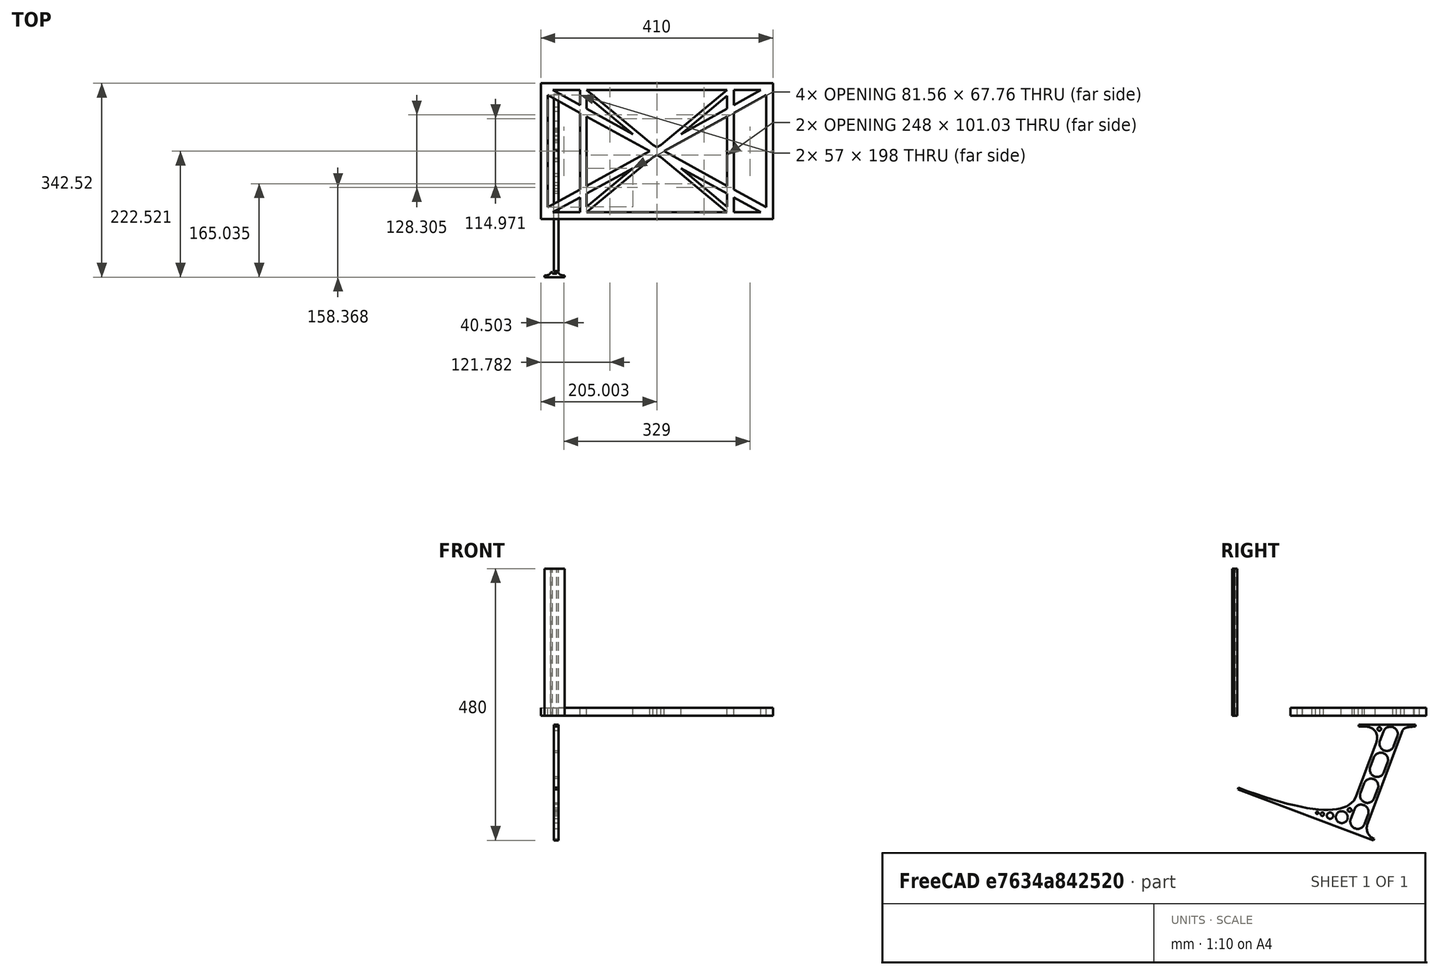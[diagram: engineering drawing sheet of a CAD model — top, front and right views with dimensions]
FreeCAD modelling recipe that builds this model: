
FCSTD DOCUMENT  (FreeCAD 0.19R0.19.2)
Label: laptopStand049
License: All rights reserved
LicenseURL: http://en.wikipedia.org/wiki/All_rights_reserved
objects: Sketcher::SketchObject×3, Part::Extrusion×3
note: 6 computed .brp shape members not serialized (recipe doc carries the construction recipe); baked Part::Feature solids carry a one-line shape summary decoded from their .brp

FEATURE [Sketcher::SketchObject] Sketch
  FullyConstrained = false
  sketch-geometry (73):
    g0: LineSegment StartX=-22.9272 StartY=136.221 StartZ=0 EndX=387.073 EndY=136.221 EndZ=0
    g1: LineSegment StartX=-22.9272 StartY=-103.779 StartZ=0 EndX=387.073 EndY=-103.779 EndZ=0
    g2: LineSegment StartX=375.073 StartY=115.221 StartZ=0 EndX=318.073 EndY=83.9235 EndZ=0
    g3: LineSegment StartX=-10.9272 StartY=-82.7794 StartZ=0 EndX=46.0728 EndY=-51.4823 EndZ=0
    g4: LineSegment StartX=-1.92719 StartY=124.221 StartZ=0 EndX=46.0728 EndY=97.8651 EndZ=0
    g5: LineSegment StartX=366.073 StartY=-91.7794 StartZ=0 EndX=318.073 EndY=-65.424 EndZ=0
    g6: LineSegment StartX=-10.9272 StartY=115.221 StartZ=0 EndX=-10.9272 EndY=-82.7794 EndZ=0
    g7: LineSegment StartX=375.073 StartY=-82.7794 StartZ=0 EndX=375.073 EndY=115.221 EndZ=0
    g8: LineSegment StartX=-1.92719 StartY=-91.7794 StartZ=0 EndX=46.0728 EndY=-91.7794 EndZ=0
    g9: LineSegment StartX=318.073 StartY=124.221 StartZ=0 EndX=366.073 EndY=124.221 EndZ=0
    g10: LineSegment StartX=306.073 StartY=-81.8102 StartZ=0 EndX=224.513 EndY=-14.0532 EndZ=0
    g11: LineSegment StartX=58.0728 StartY=114.251 StartZ=0 EndX=139.632 EndY=46.4944 EndZ=0
    g12: LineSegment StartX=306.073 StartY=124.221 StartZ=0 EndX=189.124 EndY=27.0628 EndZ=0
    g13: LineSegment StartX=58.0728 StartY=-91.7794 StartZ=0 EndX=175.022 EndY=5.37834 EndZ=0
    g14: LineSegment StartX=46.0728 StartY=124.221 StartZ=0 EndX=46.0728 EndY=97.8651 EndZ=0
    g15: LineSegment StartX=58.0728 StartY=-81.8102 StartZ=0 EndX=58.0728 EndY=-58.8351 EndZ=0
    g16: LineSegment StartX=318.073 StartY=124.221 StartZ=0 EndX=318.073 EndY=97.8651 EndZ=0
    g17: LineSegment StartX=306.073 StartY=114.251 StartZ=0 EndX=306.073 EndY=91.2763 EndZ=0
    g18: LineSegment StartX=224.513 StartY=46.4944 StartZ=0 EndX=306.073 EndY=114.251 EndZ=0
    g19: LineSegment StartX=175.022 StartY=27.0628 StartZ=0 EndX=58.0728 EndY=124.221 EndZ=0
    g20: LineSegment StartX=169.377 StartY=16.2206 StartZ=0 EndX=58.0728 EndY=77.3346 EndZ=0
    g21: LineSegment StartX=139.632 StartY=-14.0532 StartZ=0 EndX=58.0728 EndY=-81.8102 EndZ=0
    g22: LineSegment StartX=194.768 StartY=16.2206 StartZ=0 EndX=306.073 EndY=-44.8935 EndZ=0
    g23: LineSegment StartX=224.513 StartY=46.4944 StartZ=0 EndX=306.073 EndY=91.2763 EndZ=0
    g24: LineSegment StartX=175.022 StartY=27.0628 StartZ=0 EndX=179.022 EndY=24.8665 EndZ=0
    g25: LineSegment StartX=139.632 StartY=-14.0532 StartZ=0 EndX=58.0728 EndY=-58.8351 EndZ=0
    g26: LineSegment StartX=189.124 StartY=5.37834 StartZ=0 EndX=185.124 EndY=7.57463 EndZ=0
    g27: LineSegment StartX=189.124 StartY=5.37834 StartZ=0 EndX=306.073 EndY=-91.7794 EndZ=0
    g28: LineSegment StartX=306.073 StartY=77.3346 StartZ=0 EndX=306.073 EndY=-44.8935 EndZ=0
    g29: LineSegment StartX=318.073 StartY=83.9235 StartZ=0 EndX=318.073 EndY=-51.4823 EndZ=0
    g30: LineSegment StartX=318.073 StartY=97.8651 StartZ=0 EndX=366.073 EndY=124.221 EndZ=0
    g31: LineSegment StartX=306.073 StartY=77.3346 StartZ=0 EndX=194.768 EndY=16.2206 EndZ=0
    g32: LineSegment StartX=306.073 StartY=-58.8351 StartZ=0 EndX=224.513 EndY=-14.0532 EndZ=0
    g33: LineSegment StartX=306.073 StartY=-58.8351 StartZ=0 EndX=306.073 EndY=-81.8102 EndZ=0
    g34: LineSegment StartX=318.073 StartY=-51.4823 StartZ=0 EndX=375.073 EndY=-82.7794 EndZ=0
    g35: LineSegment StartX=318.073 StartY=-65.424 StartZ=0 EndX=318.073 EndY=-91.7794 EndZ=0
    g36: LineSegment StartX=318.073 StartY=-91.7794 StartZ=0 EndX=366.073 EndY=-91.7794 EndZ=0
    g37: LineSegment StartX=58.0728 StartY=-44.8935 StartZ=0 EndX=58.0728 EndY=77.3346 EndZ=0
    g38: LineSegment StartX=46.0728 StartY=-65.424 StartZ=0 EndX=-1.92719 EndY=-91.7794 EndZ=0
    g39: LineSegment StartX=46.0728 StartY=-65.424 StartZ=0 EndX=46.0728 EndY=-91.7794 EndZ=0
    g40: LineSegment StartX=58.0728 StartY=-44.8935 StartZ=0 EndX=169.377 EndY=16.2206 EndZ=0
    g41: LineSegment StartX=58.0728 StartY=91.2763 StartZ=0 EndX=58.0728 EndY=114.251 EndZ=0
    g42: LineSegment StartX=46.0728 StartY=83.9235 StartZ=0 EndX=46.0728 EndY=-51.4823 EndZ=0
    g43: LineSegment StartX=46.0728 StartY=124.221 StartZ=0 EndX=-1.92719 EndY=124.221 EndZ=0
    g44: LineSegment StartX=58.0728 StartY=91.2763 StartZ=0 EndX=139.632 EndY=46.4944 EndZ=0
    g45: LineSegment StartX=46.0728 StartY=83.9235 StartZ=0 EndX=-10.9272 EndY=115.221 EndZ=0
    g46: LineSegment StartX=-22.9272 StartY=136.221 StartZ=0 EndX=-42.9272 EndY=136.221 EndZ=0
    g47: LineSegment StartX=387.073 StartY=136.221 StartZ=0 EndX=407.073 EndY=136.221 EndZ=0
    g48: LineSegment StartX=-42.9272 StartY=136.221 StartZ=0 EndX=-42.9272 EndY=-103.779 EndZ=0
    g49: LineSegment StartX=-22.9272 StartY=-103.779 StartZ=0 EndX=-42.9272 EndY=-103.779 EndZ=0
    g50: LineSegment StartX=407.073 StartY=136.221 StartZ=0 EndX=407.073 EndY=-103.779 EndZ=0
    g51: LineSegment StartX=387.073 StartY=-103.779 StartZ=0 EndX=407.073 EndY=-103.779 EndZ=0
    g52: LineSegment StartX=179.022 StartY=27.0628 StartZ=0 EndX=179.022 EndY=124.221 EndZ=0
    g53: LineSegment StartX=185.124 StartY=27.0628 StartZ=0 EndX=185.124 EndY=124.221 EndZ=0
    g54: LineSegment StartX=179.022 StartY=27.0628 StartZ=0 EndX=179.022 EndY=24.8665 EndZ=0
    g55: LineSegment StartX=185.124 StartY=27.0628 StartZ=0 EndX=185.124 EndY=24.8665 EndZ=0
    g56: LineSegment StartX=185.124 StartY=7.57463 StartZ=0 EndX=185.124 EndY=-91.7794 EndZ=0
    g57: LineSegment StartX=179.022 StartY=7.57463 StartZ=0 EndX=179.022 EndY=-91.7794 EndZ=0
    g58: LineSegment StartX=189.124 StartY=27.0628 StartZ=0 EndX=185.124 EndY=24.8665 EndZ=0
    g59: LineSegment StartX=175.022 StartY=5.37834 StartZ=0 EndX=179.022 EndY=7.57463 EndZ=0
    g60: ArcOfCircle CenterX=-26.9272 CenterY=22.1087 CenterZ=0 NormalX=0 NormalY=0 NormalZ=1 AngleXU=0 Radius=8 StartAngle=1e-16 EndAngle=3.14159
    g61: ArcOfCircle CenterX=-26.9272 CenterY=-83.7794 CenterZ=0 NormalX=0 NormalY=0 NormalZ=1 AngleXU=0 Radius=8 StartAngle=3.14159 EndAngle=6.28319
    g62: LineSegment StartX=-34.9272 StartY=22.1087 StartZ=0 EndX=-34.9272 EndY=-83.7794 EndZ=0
    g63: LineSegment StartX=-18.9272 StartY=22.1087 StartZ=0 EndX=-18.9272 EndY=-83.7794 EndZ=0
    g64: LineSegment StartX=391.073 StartY=-91.7794 StartZ=0 EndX=391.073 EndY=-83.7794 EndZ=0
    g65: LineSegment StartX=185.124 StartY=-91.7794 StartZ=0 EndX=306.073 EndY=-91.7794 EndZ=0
    g66: LineSegment StartX=179.022 StartY=-91.7794 StartZ=0 EndX=58.0728 EndY=-91.7794 EndZ=0
    g67: LineSegment StartX=306.073 StartY=124.221 StartZ=0 EndX=185.124 EndY=124.221 EndZ=0
    g68: LineSegment StartX=179.022 StartY=124.221 StartZ=0 EndX=58.0728 EndY=124.221 EndZ=0
    g69: ArcOfCircle CenterX=451.856 CenterY=33.5494 CenterZ=0 NormalX=0 NormalY=0 NormalZ=1 AngleXU=0 Radius=8 StartAngle=-1.8e-15 EndAngle=3.14159
    g70: ArcOfCircle CenterX=451.856 CenterY=-72.3387 CenterZ=0 NormalX=0 NormalY=0 NormalZ=1 AngleXU=0 Radius=8 StartAngle=3.14159 EndAngle=6.28319
    g71: LineSegment StartX=459.856 StartY=33.5494 StartZ=0 EndX=459.856 EndY=-72.3387 EndZ=0
    g72: LineSegment StartX=443.856 StartY=33.5494 StartZ=0 EndX=443.856 EndY=-72.3387 EndZ=0
  constraints (147):
    c: Horizontal(g0)
    c: Distance(g0) = 410
    c: Horizontal(g1)
    c: Block(g0)
    c: Horizontal(g8)
    c: Horizontal(g9)
    c: Tangent(g5,g20)
    c: PointOnObject(g20,g3)
    c: PointOnObject(g22,g2)
    c: Coincident(g44,g11)
    c: Coincident(g24,g19)
    c: Coincident(g18,g23)
    c: Coincident(g25,g21)
    c: Coincident(g32,g10)
    c: Coincident(g27,g26)
    c: Coincident(g18,g17)
    c: Tangent(g17,g28)
    c: Tangent(g16,g29)
    c: Coincident(g23,g17)
    c: Tangent(g23,g30)
    c: Coincident(g2,g29)
    c: Coincident(g31,g28)
    c: Tangent(g2,g31)
    c: Coincident(g33,g10)
    c: Tangent(g5,g32)
    c: Tangent(g28,g33)
    c: Coincident(g22,g28)
    c: Tangent(g22,g34)
    c: Coincident(g29,g34)
    c: Coincident(g35,g5)
    c: Tangent(g29,g35)
    c: Coincident(g21,g15)
    c: Tangent(g15,g37)
    c: Coincident(g25,g15)
    c: Tangent(g25,g38)
    c: Coincident(g39,g38)
    c: Tangent(g14,g39)
    c: Coincident(g3,g42)
    c: Coincident(g40,g37)
    c: Tangent(g3,g40)
    c: Tangent(g37,g41)
    c: Tangent(g14,g42)
    c: Coincident(g11,g41)
    c: Coincident(g4,g14)
    c: Coincident(g44,g41)
    c: Tangent(g4,g44)
    c: Coincident(g20,g37)
    c: Coincident(g45,g42)
    c: Tangent(g20,g45)
    c: Block(g19)
    c: Block(g12)
    c: Block(g16)
    c: Block(g30)
    c: Block(g2)
    c: Block(g34)
    c: Block(g7)
    c: Block(g32)
    c: Block(g33)
    c: Block(g5)
    c: Block(g35)
    c: Block(g18)
    c: Block(g27)
    c: Block(g13)
    c: Block(g25)
    c: Block(g21)
    c: Block(g39)
    c: Block(g38)
    c: Block(g3)
    c: Block(g6)
    c: Block(g45)
    c: Block(g4)
    c: Block(g14)
    c: Block(g11)
    c: Block(g41)
    c: Block(g31)
    c: Block(g28)
    c: Block(g20)
    c: Block(g40)
    c: Block(g43)
    c: Block(g9)
    c: Block(g36)
    c: Block(g8)
    c: Horizontal(g46)
    c: Distance(g46) = 20
    c: Coincident(g47,g0)
    c: Horizontal(g47)
    c: Distance(g47) = 20
    c: Coincident(g48,g46)
    c: Vertical(g48)
    c: Horizontal(g49)
    c: Coincident(g49,g48)
    c: Coincident(g50,g47)
    c: Vertical(g50)
    c: Coincident(g51,g1)
    c: Horizontal(g51)
    c: Coincident(g51,g50)
    c: Block(g50)
    c: Block(g49)
    c: Block(g48)
    c: Block(g1)
    c: Vertical(g52)
    c: Vertical(g53)
    c: Vertical(g54)
    c: Vertical(g55)
    c: Tangent(g55,g56)
    c: Tangent(g54,g57)
    c: Coincident(g24,g54)
    c: Coincident(g26,g56)
    c: Block(g52)
    c: Block(g53)
    c: Block(g57)
    c: Block(g56)
    c: Coincident(g58,g12)
    c: Coincident(g58,g55)
    c: Coincident(g59,g13)
    c: Coincident(g59,g57)
    c: Tangent(g60,g63) = 1.5708
    c: Tangent(g60,g62) = -1.5708
    c: Tangent(g62,g61) = -1.5708
    c: Tangent(g63,g61) = 1.5708
    c: Vertical(g62)
    c: Equal(g60,g61)
    c: Block(g63)
    c: Block(g62)
    c: Vertical(g64)
    c: Distance(g64) = 8
    c: Coincident(g65,g56)
    c: Coincident(g65,g27)
    c: Horizontal(g65)
    c: Coincident(g66,g57)
    c: Coincident(g66,g13)
    c: Horizontal(g66)
    c: Coincident(g67,g12)
    c: Coincident(g67,g53)
    c: Horizontal(g67)
    c: Coincident(g68,g52)
    c: Coincident(g68,g19)
    c: Horizontal(g68)
    c: Tangent(g69,g71) = 1.5708
    c: Tangent(g71,g70) = 1.5708
    c: Equal(g69,g70)
    c: Distance(g51) = 20
    c: Distance(g1) = 410
    c: Coincident(g72,g69)
    c: Coincident(g72,g70)
    c: Vertical(g72)
    c: Block(g64)
FEATURE [Sketcher::SketchObject] Sketch001
  FullyConstrained = true
  MapMode = 4
  Placement = pos=(0,0,0) rot=(0.57735,0.57735,0.57735;2.0944rad)
  Support = -> [Sketch]
  sketch-geometry (46):
    g0: BSplineCurve PolesCount=3 KnotsCount=2 Degree=2 IsPeriodic=0
    g1: ArcOfCircle CenterX=73.122 CenterY=-32.2909 CenterZ=0 NormalX=0 NormalY=0 NormalZ=1 AngleXU=0 Radius=13 StartAngle=5.92268 EndAngle=9.06428
    g2: ArcOfCircle CenterX=66.7816 CenterY=-49.1439 CenterZ=0 NormalX=0 NormalY=0 NormalZ=1 AngleXU=0 Radius=13 StartAngle=2.78068 EndAngle=5.92131
    g3: ArcOfCircle CenterX=55.9263 CenterY=-78.1807 CenterZ=0 NormalX=0 NormalY=0 NormalZ=1 AngleXU=0 Radius=13 StartAngle=5.92268 EndAngle=9.06428
    g4: ArcOfCircle CenterX=49.5884 CenterY=-95.0342 CenterZ=0 NormalX=0 NormalY=0 NormalZ=1 AngleXU=0 Radius=13 StartAngle=2.78068 EndAngle=5.92131
    g5: ArcOfCircle CenterX=38.7206 CenterY=-124.067 CenterZ=0 NormalX=0 NormalY=0 NormalZ=1 AngleXU=0 Radius=13 StartAngle=5.92268 EndAngle=9.06428
    g6: ArcOfCircle CenterX=32.3875 CenterY=-140.92 CenterZ=0 NormalX=0 NormalY=0 NormalZ=1 AngleXU=0 Radius=13 StartAngle=2.78068 EndAngle=5.92131
    g7: ArcOfCircle CenterX=21.4715 CenterY=-169.934 CenterZ=0 NormalX=0 NormalY=0 NormalZ=1 AngleXU=0 Radius=13 StartAngle=5.92268 EndAngle=9.06428
    g8: ArcOfCircle CenterX=15.1336 CenterY=-186.787 CenterZ=0 NormalX=0 NormalY=0 NormalZ=1 AngleXU=0 Radius=13 StartAngle=2.78068 EndAngle=5.92131
    g9-g12: Circle x4 (B-spline internal-alignment scaffolding for g13; pole/knot coordinates omitted)
    g13: BSplineCurve PolesCount=4 KnotsCount=2 Degree=3 IsPeriodic=0
    g14: GeomPoint X=28.8094 Y=-19.0875 Z=0
    g15: GeomPoint X=47.0443 Y=-50.4712 Z=0
    g16: Circle CenterX=53.5586 CenterY=-23.2695 CenterZ=0 NormalX=0 NormalY=0 NormalZ=1 AngleXU=0 Radius=3.24518
    g17: Circle CenterX=-195.441 CenterY=-127.082 CenterZ=0 NormalX=0 NormalY=0 NormalZ=1 AngleXU=0 Radius=1
    g18: Circle CenterX=-8.24091 CenterY=-197.481 CenterZ=0 NormalX=0 NormalY=0 NormalZ=1 AngleXU=0 Radius=1
    g19: Circle CenterX=12.8789 CenterY=-141.321 CenterZ=0 NormalX=0 NormalY=0 NormalZ=1 AngleXU=0 Radius=1
    g20: BSplineCurve PolesCount=3 KnotsCount=2 Degree=2 IsPeriodic=0
    g21: GeomPoint X=-195.441 Y=-127.082 Z=0
    g22: GeomPoint X=12.8789 Y=-141.321 Z=0
    g23: Circle CenterX=-12.8016 CenterY=-179.036 CenterZ=0 NormalX=0 NormalY=0 NormalZ=1 AngleXU=0 Radius=10.5072
    g24: Circle CenterX=0.933922 CenterY=-166.43 CenterZ=0 NormalX=0 NormalY=0 NormalZ=1 AngleXU=0 Radius=3.26661
    g25: Circle CenterX=-33.5518 CenterY=-176.44 CenterZ=0 NormalX=0 NormalY=0 NormalZ=1 AngleXU=0 Radius=5.64388
    g26: Circle CenterX=-47.2366 CenterY=-173.859 CenterZ=0 NormalX=0 NormalY=0 NormalZ=1 AngleXU=0 Radius=3.01653
    g27: Circle CenterX=-56.2595 CenterY=-171.456 CenterZ=0 NormalX=0 NormalY=0 NormalZ=1 AngleXU=0 Radius=2.12826
    g28: ArcOfCircle CenterX=51.2151 CenterY=-198.473 CenterZ=0 NormalX=0 NormalY=0 NormalZ=1 AngleXU=0 Radius=20 StartAngle=2.78189 EndAngle=4.35269
    g29: LineSegment StartX=32.4951 StartY=-191.433 StartZ=0 EndX=94.6577 EndY=-26.1351 EndZ=0
    g30: LineSegment StartX=43.1192 StartY=-220.001 StartZ=0 EndX=-196.497 EndY=-129.89 EndZ=0
    g31: LineSegment StartX=43.1192 StartY=-220.001 StartZ=0 EndX=44.1752 EndY=-217.193 EndZ=0
    g32: LineSegment StartX=117.223 StartY=-19.0875 StartZ=0 EndX=117.223 EndY=-16.0875 EndZ=0
    g33: LineSegment StartX=117.223 StartY=-16.0875 StartZ=0 EndX=17.2232 EndY=-16.0875 EndZ=0
    g34: LineSegment StartX=17.2232 StartY=-16.0875 StartZ=0 EndX=17.2232 EndY=-19.0875 EndZ=0
    g35: LineSegment StartX=28.8094 StartY=-19.0875 StartZ=0 EndX=17.2232 EndY=-19.0875 EndZ=0
    g36: LineSegment StartX=47.0443 StartY=-50.4712 StartZ=0 EndX=12.8789 EndY=-141.321 EndZ=0
    g37: LineSegment StartX=-195.441 StartY=-127.082 StartZ=0 EndX=-196.497 EndY=-129.89 EndZ=0
    g38: LineSegment StartX=85.2864 StartY=-36.8765 StartZ=0 EndX=78.9396 EndY=-53.7463 EndZ=0
    g39: LineSegment StartX=60.9577 StartY=-27.7052 StartZ=0 EndX=54.6191 EndY=-44.5532 EndZ=0
    g40: LineSegment StartX=68.0907 StartY=-82.7664 StartZ=0 EndX=61.7465 EndY=-99.6365 EndZ=0
    g41: LineSegment StartX=43.7619 StartY=-73.595 StartZ=0 EndX=37.426 EndY=-90.4435 EndZ=0
    g42: LineSegment StartX=50.885 StartY=-128.652 StartZ=0 EndX=44.5456 EndY=-145.522 EndZ=0
    g43: LineSegment StartX=26.5562 StartY=-119.481 StartZ=0 EndX=20.2251 EndY=-136.329 EndZ=0
    g44: LineSegment StartX=9.3071 StartY=-165.349 StartZ=0 EndX=2.97115 EndY=-182.197 EndZ=0
    g45: LineSegment StartX=33.6358 StartY=-174.52 StartZ=0 EndX=27.2917 EndY=-191.39 EndZ=0
  constraints (70):
    c: Block(g0)
    c: Block(g1)
    c: Block(g2)
    c: Block(g4)
    c: Block(g3)
    c: Block(g6)
    c: Block(g5)
    c: Block(g8)
    c: Block(g7)
    c: Weight(g9) = 1
    c: Equal(g9,g10)
    c: Equal(g9,g11)
    c: Equal(g9,g12)
    c: InternalAlignment(g9-g12 -> g13) x4
    c: InternalAlignment(g14,g13)
    c: InternalAlignment(g15,g13)
    c: Block(g16)
    c: Weight(g17) = 1
    c: Equal(g17,g18)
    c: Equal(g17,g19)
    c: InternalAlignment(g17,g20)
    c: InternalAlignment(g18,g20)
    c: InternalAlignment(g19,g20)
    c: InternalAlignment(g21,g20)
    c: InternalAlignment(g22,g20)
    c: Block(g20)
    c: Block(g23)
    c: Block(g24)
    c: Block(g25)
    c: Block(g26)
    c: Block(g27)
    c: Block(g28)
    c: Coincident(g29,g28)
    c: Coincident(g29,g0)
    c: Block(g13)
    c: Coincident(g31,g30)
    c: Coincident(g31,g28)
    c: Block(g31)
    c: Coincident(g32,g0)
    c: Vertical(g32)
    c: Coincident(g33,g32)
    c: Horizontal(g33)
    c: Coincident(g34,g33)
    c: Vertical(g34)
    c: Block(g33)
    c: Coincident(g35,g13)
    c: Coincident(g35,g34)
    c: Horizontal(g35)
    c: Coincident(g36,g13)
    c: Coincident(g36,g20)
    c: Coincident(g37,g20)
    c: Coincident(g37,g30)
    c: Block(g30)
    c: Coincident(g38,g1)
    c: Coincident(g38,g2)
    c: Coincident(g39,g1)
    c: Coincident(g39,g2)
    c: Coincident(g40,g3)
    c: Coincident(g40,g4)
    c: Coincident(g41,g3)
    c: Coincident(g41,g4)
    c: Coincident(g42,g5)
    c: Coincident(g42,g6)
    c: Coincident(g43,g5)
    c: Coincident(g43,g6)
    c: Coincident(g44,g7)
    c: Coincident(g44,g8)
    c: Coincident(g45,g7)
    c: Coincident(g45,g8)
    c: Distance(g30) = 256
FEATURE [Part::Extrusion] Extrude002
  Base = -> Sketch001
  Dir = (1,0,0)
  DirMode = 2
  FaceMakerClass = Part::FaceMakerBullseye
  LengthFwd = 8
  LengthRev = 0
  Solid = true
  Symmetric = false
FEATURE [Sketcher::SketchObject] Sketch002
  FullyConstrained = true
  sketch-geometry (20):
    g0: LineSegment StartX=-2.77179 StartY=-200.304 StartZ=0 EndX=5.22821 EndY=-200.304 EndZ=0
    g1: LineSegment StartX=5.22821 StartY=-200.304 StartZ=0 EndX=5.22821 EndY=-197.304 EndZ=0
    g2: LineSegment StartX=-2.77179 StartY=-200.304 StartZ=0 EndX=-2.77179 EndY=-197.304 EndZ=0
    g3: LineSegment StartX=5.22821 StartY=-197.304 StartZ=0 EndX=8.22821 EndY=-197.304 EndZ=0
    g4: LineSegment StartX=-2.77179 StartY=-197.304 StartZ=0 EndX=-5.77179 EndY=-197.304 EndZ=0
    g5: LineSegment StartX=19.2282 StartY=-203.304 StartZ=0 EndX=19.2282 EndY=-206.304 EndZ=0
    g6: LineSegment StartX=-16.7718 StartY=-203.304 StartZ=0 EndX=-16.7718 EndY=-206.304 EndZ=0
    g7: LineSegment StartX=-16.7718 StartY=-206.304 StartZ=0 EndX=19.2282 EndY=-206.304 EndZ=0
    g8: Circle CenterX=-16.7718 CenterY=-203.304 CenterZ=0 NormalX=0 NormalY=0 NormalZ=1 AngleXU=0 Radius=1
    g9: Circle CenterX=-5.77179 CenterY=-203.304 CenterZ=0 NormalX=0 NormalY=0 NormalZ=1 AngleXU=0 Radius=1
    g10: Circle CenterX=-5.77179 CenterY=-197.304 CenterZ=0 NormalX=0 NormalY=0 NormalZ=1 AngleXU=0 Radius=1
    g11: BSplineCurve PolesCount=3 KnotsCount=2 Degree=2 IsPeriodic=0
    g12: GeomPoint X=-16.7718 Y=-203.304 Z=0
    g13: GeomPoint X=-5.77179 Y=-197.304 Z=0
    g14: Circle CenterX=19.2282 CenterY=-203.304 CenterZ=0 NormalX=0 NormalY=0 NormalZ=1 AngleXU=0 Radius=1
    g15: Circle CenterX=8.22821 CenterY=-203.304 CenterZ=0 NormalX=0 NormalY=0 NormalZ=1 AngleXU=0 Radius=1
    g16: Circle CenterX=8.22821 CenterY=-197.304 CenterZ=0 NormalX=0 NormalY=0 NormalZ=1 AngleXU=0 Radius=1
    g17: BSplineCurve PolesCount=3 KnotsCount=2 Degree=2 IsPeriodic=0
    g18: GeomPoint X=19.2282 Y=-203.304 Z=0
    g19: GeomPoint X=8.22821 Y=-197.304 Z=0
  constraints (41):
    c: Horizontal(g0)
    c: Distance(g0) = 8
    c: Coincident(g1,g0)
    c: Vertical(g1)
    c: Distance(g1) = 3
    c: Coincident(g2,g0)
    c: Vertical(g2)
    c: Distance(g2) = 3
    c: Coincident(g3,g1)
    c: Horizontal(g3)
    c: Distance(g3) = 3
    c: Coincident(g4,g2)
    c: Horizontal(g4)
    c: Distance(g4) = 3
    c: Vertical(g5)
    c: Vertical(g6)
    c: Coincident(g7,g6)
    c: Coincident(g7,g5)
    c: Weight(g8) = 1
    c: Equal(g8,g9)
    c: Equal(g8,g10)
    c: Coincident(g11,g4)
    c: InternalAlignment(g8,g11)
    c: InternalAlignment(g9,g11)
    c: InternalAlignment(g10,g11)
    c: InternalAlignment(g12,g11)
    c: InternalAlignment(g13,g11)
    c: Coincident(g17,g5)
    c: Weight(g14) = 1
    c: Equal(g14,g15)
    c: Equal(g14,g16)
    c: Coincident(g17,g3)
    c: InternalAlignment(g14,g17)
    c: InternalAlignment(g15,g17)
    c: InternalAlignment(g16,g17)
    c: InternalAlignment(g18,g17)
    c: InternalAlignment(g19,g17)
    c: Block(g7)
    c: Block(g17)
    c: Block(g11)
    c: Block(g6)
FEATURE [Part::Extrusion] Extrude003
  Base = -> Sketch002
  Dir = (0,0,1)
  DirMode = 2
  FaceMakerClass = Part::FaceMakerBullseye
  LengthFwd = 260
  LengthRev = 0
  Solid = true
  Symmetric = false
FEATURE [Part::Extrusion] Extrude
  Base = -> Sketch
  Dir = (0,0,1)
  DirMode = 2
  FaceMakerClass = Part::FaceMakerBullseye
  LengthFwd = 14
  LengthRev = 0
  Solid = true
  Symmetric = false
